# Revit family: BVN_ARMO-JP
name_source: partatom
category: Mechanical Equipment
units: mm (PartAtom-declared; Revit-internal decimal feet)

## family parameters
Always vertical = Yes
Cut with Voids When Loaded = No
OmniClass Number = 23.75.00.00
OmniClass Title = Climate Control (HVAC)
Part Type = Normal
Room Calculation Point = No
Round Connector Dimension = Use Diameter
Shared = No
Work Plane-Based = No

## types (6) — shared parameters
A' = 150 mm
Description = Smoke Exhaust Fan
Dis Malzeme = <By Category>
Ic Malzeme = <By Category>
Manufacturer = BVN
Model = ARMO-JF
Tij Malzeme = <By Category>
URL = http://www.bahcivanmotor.com.tr

## per-type parameters (varying)
- ARMO-JF-315 RDA: A=1600 mm  [stored 5.24934 ft]; Air Flow=4500.0 m³/h; B=390 mm  [stored 1.27953 ft]; C=360 mm  [stored 1.1811 ft]; Current=2 A; D=315 mm  [stored 1.03346 ft]; E=310 mm  [stored 1.01706 ft]; F=275 mm; Frequency=50 Hz; G=375 mm  [stored 1.23031 ft]; H=400 mm  [stored 1.31234 ft]; Insulation Class=H; Power=800 W; Protection Class=55; R=Yes; Sound Pressure Level dB(A)=62; Speed (rpm)=2810; Thrust=24 N; Voltage=400 V; Weight=93.00 kg; b=195 mm  [stored 0.639764 ft]; c=180 mm; e=125 mm  [stored 0.410105 ft]; g=188 mm; g'=-188 mm; y=48 mm
- ARMO-JF-355 UDA: A=1700 mm  [stored 5.57743 ft]; Air Flow=6900.0 m³/h; B=455 mm; C=410 mm  [stored 1.34514 ft]; Current=2 A; D=355 mm; E=360 mm  [stored 1.1811 ft]; F=275 mm; Frequency=50 Hz; G=375 mm  [stored 1.23031 ft]; H=465 mm; Insulation Class=H; Power=1100 W; Protection Class=55; R=No; Sound Pressure Level dB(A)=70; Speed (rpm)=2900; Thrust=45 N; Voltage=400 V; Weight=98.00 kg; b=228 mm; c=205 mm  [stored 0.672572 ft]; e=135 mm  [stored 0.442913 ft]; g=188 mm; g'=-188 mm; y=64 mm
- ARMO-JF-400 UDA: A=1850 mm  [stored 6.06955 ft]; Air Flow=10872.0 m³/h; B=500 mm  [stored 1.64042 ft]; C=450 mm  [stored 1.47638 ft]; Current=5 A; D=400 mm  [stored 1.31234 ft]; E=400 mm  [stored 1.31234 ft]; F=350 mm  [stored 1.14829 ft]; Frequency=0 Hz; G=450 mm  [stored 1.47638 ft]; H=510 mm; Power=2500 W; Protection Class=0; R=No; Sound Pressure Level dB(A)=72; Speed (rpm)=2845; Thrust=86 N; Voltage=0 V; Weight=105.00 kg; b=250 mm  [stored 0.82021 ft]; c=225 mm  [stored 0.738189 ft]; e=150 mm; g=225 mm  [stored 0.738189 ft]; g'=-225 mm  [stored -0.738189 ft]; y=75 mm
- ARMO-JF-315 UDA: A=1600 mm  [stored 5.24934 ft]; Air Flow=4600.0 m³/h; B=390 mm  [stored 1.27953 ft]; C=360 mm  [stored 1.1811 ft]; Current=2 A; D=315 mm  [stored 1.03346 ft]; E=310 mm  [stored 1.01706 ft]; F=275 mm; Frequency=50 Hz; G=375 mm  [stored 1.23031 ft]; H=400 mm  [stored 1.31234 ft]; Insulation Class=H; Power=800 W; Protection Class=55; R=No; Sound Pressure Level dB(A)=66; Speed (rpm)=2810; Thrust=25 N; Voltage=400 V; Weight=91.00 kg; b=195 mm  [stored 0.639764 ft]; c=180 mm; e=125 mm  [stored 0.410105 ft]; g=188 mm; g'=-188 mm; y=48 mm
- ARMO-JF-355 RDA: A=1700 mm  [stored 5.57743 ft]; Air Flow=6540.0 m³/h; B=455 mm; C=410 mm  [stored 1.34514 ft]; Current=2 A; D=355 mm; E=360 mm  [stored 1.1811 ft]; F=275 mm; Frequency=50 Hz; G=375 mm  [stored 1.23031 ft]; H=465 mm; Insulation Class=H; Power=1100 W; Protection Class=55; R=Yes; Sound Pressure Level dB(A)=66; Speed (rpm)=2900; Thrust=41 N; Voltage=400 V; Weight=100.00 kg; b=228 mm; c=205 mm  [stored 0.672572 ft]; e=135 mm  [stored 0.442913 ft]; g=188 mm; g'=-188 mm; y=64 mm
- ARMO-JF-400 RDA: A=1850 mm  [stored 6.06955 ft]; Air Flow=9750.0 m³/h; B=500 mm  [stored 1.64042 ft]; C=450 mm  [stored 1.47638 ft]; Current=3 A; D=400 mm  [stored 1.31234 ft]; E=400 mm  [stored 1.31234 ft]; F=350 mm  [stored 1.14829 ft]; Frequency=50 Hz; G=450 mm  [stored 1.47638 ft]; H=510 mm; Insulation Class=H; Power=1500 W; Protection Class=55; R=Yes; Sound Pressure Level dB(A)=68; Speed (rpm)=2845; Thrust=70 N; Voltage=400 V; Weight=107.00 kg; b=250 mm  [stored 0.82021 ft]; c=225 mm  [stored 0.738189 ft]; e=150 mm; g=225 mm  [stored 0.738189 ft]; g'=-225 mm  [stored -0.738189 ft]; y=75 mm

note: [stored X ft] marks values corroborated as IEEE doubles in the binary element streams (Revit-internal decimal feet)

## geometry (parser evidence)
native form markers: Sweep x2
no freeform markers — native parametric forms only
